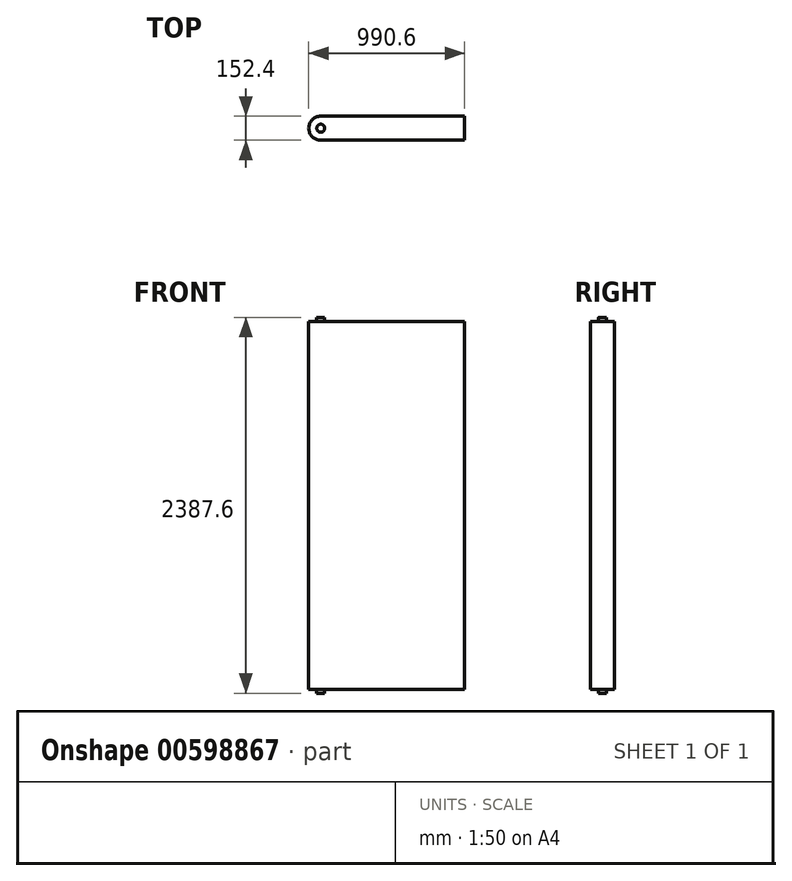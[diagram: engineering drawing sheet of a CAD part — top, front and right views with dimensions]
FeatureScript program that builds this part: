
annotation { "Feature Type Name" : "Feature", "Feature Type Description" : "" }
export const myFeature = defineFeature(function(context is Context, id is Id, definition is map)
    precondition{}
    {
        {
            var Q0;
            Q0=qCreatedBy(makeId("Top.planeOp"),FACE);
            var sketch = newSketch(context, id + "F0", { "sketchPlane" : qUnion([Q0])});
            skLineSegment(sketch, "E0.bottom", {"start": v(495.3, 180.34) * mm, "end": v(-495.3, 180.34) * mm});
            skLineSegment(sketch, "E0.top", {"start": v(495.3, 27.94) * mm, "end": v(-495.3, 27.94) * mm});
            skLineSegment(sketch, "E0.left", {"start": v(495.3, 180.34) * mm, "end": v(495.3, 27.94) * mm});
            skLineSegment(sketch, "E0.right", {"start": v(-495.3, 180.34) * mm, "end": v(-495.3, 27.94) * mm});
            skPoint(sketch, "E0.middle", {"position": v(0, 104.14) * mm});
            skSolve(sketch);
        }
        {
            var Q0;
            Q0=makeQuery(id+"F0.imprint","IMPRINT",FACE,{"disambiguationData":[TD([[makeQuery(id+"F0.imprint","IMPRINT",EDGE,{"derivedFrom":sQuery(id+"F0.wireOp",EDGE,"E0.bottom")}),1.0]])]});
            extrude(context, id + "F1", {"entities" : qUnion([Q0]), "depth" : 2336.8 * mm, "offsetDistance" : 25.4 * mm});
        }
        {
            var Q0;
            Q0=makeQuery(id+"F1.opExtrude","CAP_FACE",FACE,{"disambiguationData":[OSD([sQuery(id+"F0.wireOp",EDGE,"E0.bottom"),sQuery(id+"F0.wireOp",EDGE,"E0.top"),sQuery(id+"F0.wireOp",EDGE,"E0.left"),sQuery(id+"F0.wireOp",EDGE,"E0.right")])],"isStart":false});
            var sketch = newSketch(context, id + "F2", { "sketchPlane" : qUnion([Q0])});
            skLineSegment(sketch, "E1.bottom", {"start": v(-495.3, 180.34) * mm, "end": v(-419.1, 180.34) * mm});
            skLineSegment(sketch, "E1.top", {"start": v(-495.3, 104.14) * mm, "end": v(-419.1, 104.14) * mm});
            skLineSegment(sketch, "E1.left", {"start": v(-495.3, 180.34) * mm, "end": v(-495.3, 104.14) * mm});
            skLineSegment(sketch, "E1.right", {"start": v(-419.1, 180.34) * mm, "end": v(-419.1, 104.14) * mm});
            skCircle(sketch, "E2", {"center": v(-419.1, 104.14) * mm, "radius": 25.4 * mm});
            skSolve(sketch);
        }
        {
            var Q0;
            {var subQ0=sQuery(id+"F2.wireOp",EDGE,"E1.right");var subQ1=sQuery(id+"F2.wireOp",EDGE,"E1.top");var subQ2=makeQuery(id+"F2.imprint","INTERSECT",VERTEX,{"derivedFrom":[subQ1,subQ0]});Q0=makeQuery(id+"F2.imprint","IMPRINT",FACE,{"disambiguationData":[TD([[makeQuery(id+"F2.imprint","IMPRINT",EDGE,{"disambiguationData":[TD([[subQ2,1.0]])],"derivedFrom":subQ1}),1.0]])]});}
            var Q1;
            {var subQ0=sQuery(id+"F2.wireOp",EDGE,"E1.right");var subQ1=sQuery(id+"F2.wireOp",EDGE,"E1.top");var subQ2=makeQuery(id+"F2.imprint","INTERSECT",VERTEX,{"derivedFrom":[subQ1,subQ0]});Q1=makeQuery(id+"F2.imprint","IMPRINT",FACE,{"disambiguationData":[TD([[makeQuery(id+"F2.imprint","IMPRINT",EDGE,{"disambiguationData":[TD([[subQ2,1.0]])],"derivedFrom":subQ1}),-1.0]])]});}
            extrude(context, id + "F3", {"entities" : qUnion([Q0, Q1]), "operationType" : NewBodyOperationType.ADD, "depth" : 25.4 * mm, "offsetDistance" : 25.4 * mm});
        }
        {
            var Q0;
            Q0=makeQuery(id+"F1.opExtrude","CAP_FACE",FACE,{"disambiguationData":[OSD([sQuery(id+"F0.wireOp",EDGE,"E0.bottom"),sQuery(id+"F0.wireOp",EDGE,"E0.top"),sQuery(id+"F0.wireOp",EDGE,"E0.left"),sQuery(id+"F0.wireOp",EDGE,"E0.right")])],"isStart":true});
            var sketch = newSketch(context, id + "F4", { "sketchPlane" : qUnion([Q0])});
            skLineSegment(sketch, "E3.bottom", {"start": v(-495.3, -27.94) * mm, "end": v(-419.1, -27.94) * mm});
            skLineSegment(sketch, "E3.top", {"start": v(-495.3, -104.14) * mm, "end": v(-419.1, -104.14) * mm});
            skLineSegment(sketch, "E3.left", {"start": v(-495.3, -27.94) * mm, "end": v(-495.3, -104.14) * mm});
            skLineSegment(sketch, "E3.right", {"start": v(-419.1, -27.94) * mm, "end": v(-419.1, -104.14) * mm});
            skCircle(sketch, "E4", {"center": v(-419.1, -104.14) * mm, "radius": 25.4 * mm});
            skSolve(sketch);
        }
        {
            var Q0;
            {var subQ0=sQuery(id+"F4.wireOp",EDGE,"E3.right");var subQ1=sQuery(id+"F4.wireOp",EDGE,"E3.top");var subQ2=makeQuery(id+"F4.imprint","INTERSECT",VERTEX,{"derivedFrom":[subQ1,subQ0]});Q0=makeQuery(id+"F4.imprint","IMPRINT",FACE,{"disambiguationData":[TD([[makeQuery(id+"F4.imprint","IMPRINT",EDGE,{"disambiguationData":[TD([[subQ2,1.0]])],"derivedFrom":subQ1}),1.0]])]});}
            var Q1;
            {var subQ0=sQuery(id+"F4.wireOp",EDGE,"E3.right");var subQ1=sQuery(id+"F4.wireOp",EDGE,"E3.top");var subQ2=makeQuery(id+"F4.imprint","INTERSECT",VERTEX,{"derivedFrom":[subQ1,subQ0]});Q1=makeQuery(id+"F4.imprint","IMPRINT",FACE,{"disambiguationData":[TD([[makeQuery(id+"F4.imprint","IMPRINT",EDGE,{"disambiguationData":[TD([[subQ2,1.0]])],"derivedFrom":subQ1}),-1.0]])]});}
            extrude(context, id + "F5", {"entities" : qUnion([Q0, Q1]), "operationType" : NewBodyOperationType.ADD, "depth" : 25.4 * mm, "offsetDistance" : 25.4 * mm});
        }
        {
            var Q0;
            Q0=makeQuery(id+"F1.opExtrude","CAP_FACE",FACE,{"disambiguationData":[OSD([sQuery(id+"F0.wireOp",EDGE,"E0.bottom"),sQuery(id+"F0.wireOp",EDGE,"E0.top"),sQuery(id+"F0.wireOp",EDGE,"E0.left"),sQuery(id+"F0.wireOp",EDGE,"E0.right")])],"isStart":false});
            var sketch = newSketch(context, id + "F6", { "sketchPlane" : qUnion([Q0])});
            skCircle(sketch, "E5", {"center": v(-419.1, 104.14) * mm, "radius": 76.2 * mm});
            skSolve(sketch);
        }
        {
            var Q0;
            {var subQ0=sQuery(id+"F6.wireOp",EDGE,"E5");var subQ1=makeQuery(id+"F1.opExtrude","CAP_EDGE",EDGE,{"disambiguationData":[OSD([sQuery(id+"F0.wireOp",EDGE,"E0.right")])],"isStart":false});var subQ2=makeQuery(id+"F6.imprint","INTERSECT",VERTEX,{"derivedFrom":[subQ1,subQ0]});Q0=makeQuery(id+"F6.imprint","IMPRINT",FACE,{"disambiguationData":[TD([[makeQuery(id+"F6.imprint","IMPRINT",EDGE,{"disambiguationData":[TD([[subQ2,1.0]])],"derivedFrom":subQ0}),-1.0]])]});}
            var Q1;
            {var subQ0=sQuery(id+"F6.wireOp",EDGE,"E5");var subQ1=makeQuery(id+"F1.opExtrude","CAP_EDGE",EDGE,{"disambiguationData":[OSD([sQuery(id+"F0.wireOp",EDGE,"E0.right")])],"isStart":false});var subQ2=makeQuery(id+"F6.imprint","INTERSECT",VERTEX,{"derivedFrom":[subQ1,subQ0]});Q1=makeQuery(id+"F6.imprint","IMPRINT",FACE,{"disambiguationData":[TD([[makeQuery(id+"F6.imprint","IMPRINT",EDGE,{"disambiguationData":[TD([[subQ2,-1.0]])],"derivedFrom":subQ0}),-1.0]])]});}
            extrude(context, id + "F7", {"entities" : qUnion([Q0, Q1]), "operationType" : NewBodyOperationType.REMOVE, "oppositeDirection" : true, "depth" : 2387.6 * mm, "offsetDistance" : 25.4 * mm});
        }
    });
